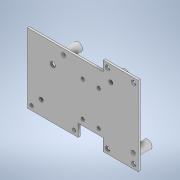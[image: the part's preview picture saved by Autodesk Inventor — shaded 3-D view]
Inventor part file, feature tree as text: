
AUTODESK INVENTOR PART (.ipt)
format: ipt  version: 2021 (Build 250183000, 183)  size: 1,264,128 bytes
history: native  units: mm
features: reference x24, other x9, sketch x6, extrude x3, plane x2, chamfer x2
ambient origin geometry x8: Origin, YZ Plane, XZ Plane, XY Plane, X Axis, Y Axis, Z Axis, Center Point
bodies: Volumenkörper1 (feature_tree)
feature tree (46):
  plane  "Arbeitsebene1"
  extrude  "Extrusion1"  Depth=1.0mm
  extrude  "Extrusion2"  Depth=1.0mm
  plane  "Arbeitsebene2"
  chamfer  "Fase1"  Distance=1.0mm
  sketch  "Skizze6"  dims[d6=1.0mm]
  other  "Spirale1"
  sketch  "Skizzenbasierte Anordnung1"  dims[d0=1.0mm d1=1.0mm]
  chamfer  "Fase2"  Distance=1.0mm
  extrude  "Extrusion3"  Depth=1.6mm TaperAngle=0.0deg
  sketch  "Skizze1"  dims[d2=1.0mm d3=1.0mm]
  reference  "Referenz1"
  reference  "Referenz2"
  reference  "Referenz3"
  reference  "Referenz4"
  reference  "Referenz5"
  reference  "Referenz6"
  reference  "Referenz7"
  reference  "Referenz8"
  reference  "Referenz9"
  reference  "Referenz10"
  reference  "Referenz11"
  reference  "Referenz12"
  reference  "Referenz13"
  reference  "Referenz14"
  reference  "Referenz15"
  reference  "Referenz16"
  reference  "Referenz17"
  reference  "Referenz18"
  reference  "Referenz19"
  reference  "Referenz20"
  reference  "Referenz21"
  reference  "Referenz22"
  reference  "Referenz23"
  reference  "Referenz24"
  sketch  "Skizze2"  dims[d4=1.0mm]
  other  "Arbeitsachse1"
  sketch  "Skizze5"  dims[d5=1.0mm]
  sketch  "Skizze7"  dims[d7=2.0mm d8=1.0mm d9=1.0mm d10=1.6mm d11=0.0mm d16=10.0mm d17=0.0mm d18=2.0mm d19=0.2mm d20=0.2mm d21=0.2mm d22=2.0mm d23=2.0mm d24=2.0mm d25=2.0mm d26=2.0mm d27=0.2mm d28=0.2mm d29=3.1505mm d30=1.92mm d31=1.92mm d32=1.92mm d33=1.92mm d34=60.0deg d35=3.8mm d36=0.6mm d37=3.1505mm d38=0.32475mm d39=0.06495mm d40=60.0deg d41=3.8mm d42=0.6mm d43=3.1505mm d44=0.5196mm d45=0.6mm d46=10.0mm d47=10.0mm d48=0.0mm d49=90.0deg d50=90.0deg d51=0.0mm d52=0.0mm d53=0.5mm d54=2.0mm d55=45.0deg d56=1.0mm d57=1.0mm d58=1.0mm d59=1.0mm d60=1.0mm d61=1.0mm d62=1.0mm d63=1.0mm d64=1.0mm d65=1.0mm d66=1.0mm d67=2.0mm d68=0.0mm d69=0.4mm d70=2.0mm d71=45.0deg]
  other  "<userpath>\Desktop\Bachelorarbeit\CAD\00_RobotAssembly.iam"
  other  "00_RobotAssembly.iam"
  other  "01_CaseBottom:1"
  other  "dc-dc-5a-cc:1"
  other  "PCB^dc-dc-5a-cc_1"
  other  "PCB_PowerSupply:1"
  other  "Step_Down_USB:1"
